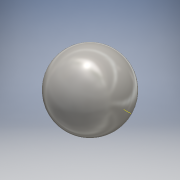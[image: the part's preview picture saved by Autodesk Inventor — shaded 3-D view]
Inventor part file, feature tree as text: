
AUTODESK INVENTOR PART (.ipt)
format: ipt  version: 2016 (Build 200138000, 138)  size: 130,560 bytes
history: native  units: mm
features: sketch x3, extrude x2, fillet x2, revolve x1, plane x1
ambient origin geometry x8: Origin, YZ Plane, XZ Plane, XY Plane, X Axis, Y Axis, Z Axis, Center Point
bodies: Solid1 (feature_tree)
feature tree (9):
  revolve  "Revolution1"  Angle=90.0deg
  plane  "Work Plane1"
  extrude  "Extrusion1"  Depth=9.0mm
  extrude  "Extrusion2"  Depth=5.0mm
  fillet  "Fillet1"  Radius=5.0mm
  fillet  "Fillet2"  Radius=0.5mm
  sketch  "Sketch1"  dims[d0=10.0mm d1=90.0deg]
  sketch  "Sketch2"  dims[d2=4.0mm d3=9.0mm]
  sketch  "Sketch3"  dims[d4=5.0mm d5=0.0mm d6=5.0mm d7=5.0mm d8=0.0mm d9=0.5mm d10=0.5mm]
